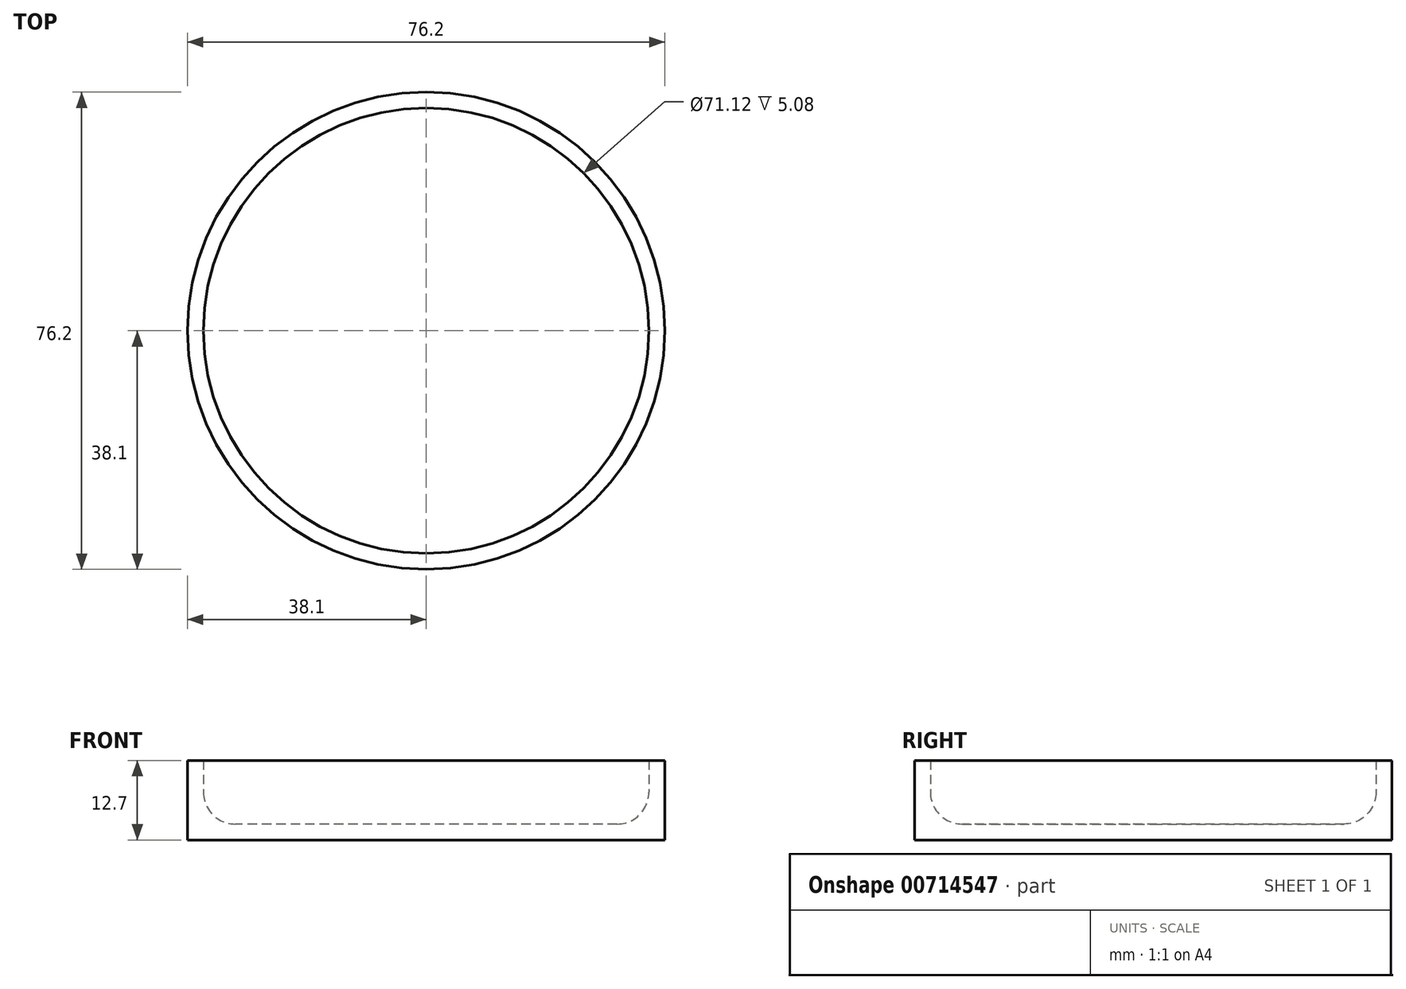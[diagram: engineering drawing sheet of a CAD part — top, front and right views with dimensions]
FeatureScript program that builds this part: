
annotation { "Feature Type Name" : "Feature", "Feature Type Description" : "" }
export const myFeature = defineFeature(function(context is Context, id is Id, definition is map)
    precondition{}
    {
        {
            var Q0;
            Q0=qCreatedBy(makeId("Top.planeOp"),FACE);
            var sketch = newSketch(context, id + "F0", { "sketchPlane" : qUnion([Q0])});
            skCircle(sketch, "E0", {"center": v(0, 0) * mm, "radius": 38.1 * mm});
            skSolve(sketch);
        }
        {
            var Q0;
            Q0=makeQuery(id+"F0.imprint","IMPRINT",FACE,{"disambiguationData":[TD([[makeQuery(id+"F0.imprint","IMPRINT",EDGE,{"derivedFrom":sQuery(id+"F0.wireOp",EDGE,"E0")}),1.0]])]});
            extrude(context, id + "F1", {"entities" : qUnion([Q0]), "endBound" : BoundingType.SYMMETRIC, "depth" : 12.7 * mm, "offsetDistance" : 25.4 * mm});
        }
        {
            var Q0;
            Q0=makeQuery(id+"F1.opExtrude","CAP_FACE",FACE,{"disambiguationData":[OSD([sQuery(id+"F0.wireOp",EDGE,"E0")])],"isStart":false});
            shell(context, id + "F2", {"entities" : qUnion([Q0]), "thickness" : 2.54 * mm});
        }
        {
            var Q0;
            {var subQ0=sQuery(id+"F0.wireOp",EDGE,"E0");Q0=makeQuery(id+"F2.opShell","OFFSET_EDGE",EDGE,{"disambiguationData":[OSD([subQ0]),TDD([makeQuery(id+"F1.opExtrude","CAP_EDGE",EDGE,{"disambiguationData":[OSD([subQ0])],"isStart":true})])]});}
            fillet(context, id + "F3", {"entities" : qUnion([Q0]), "radius" : 5.08 * mm, "tangentPropagation" : true, "allowEdgeOverflow" : false});
        }
    });
